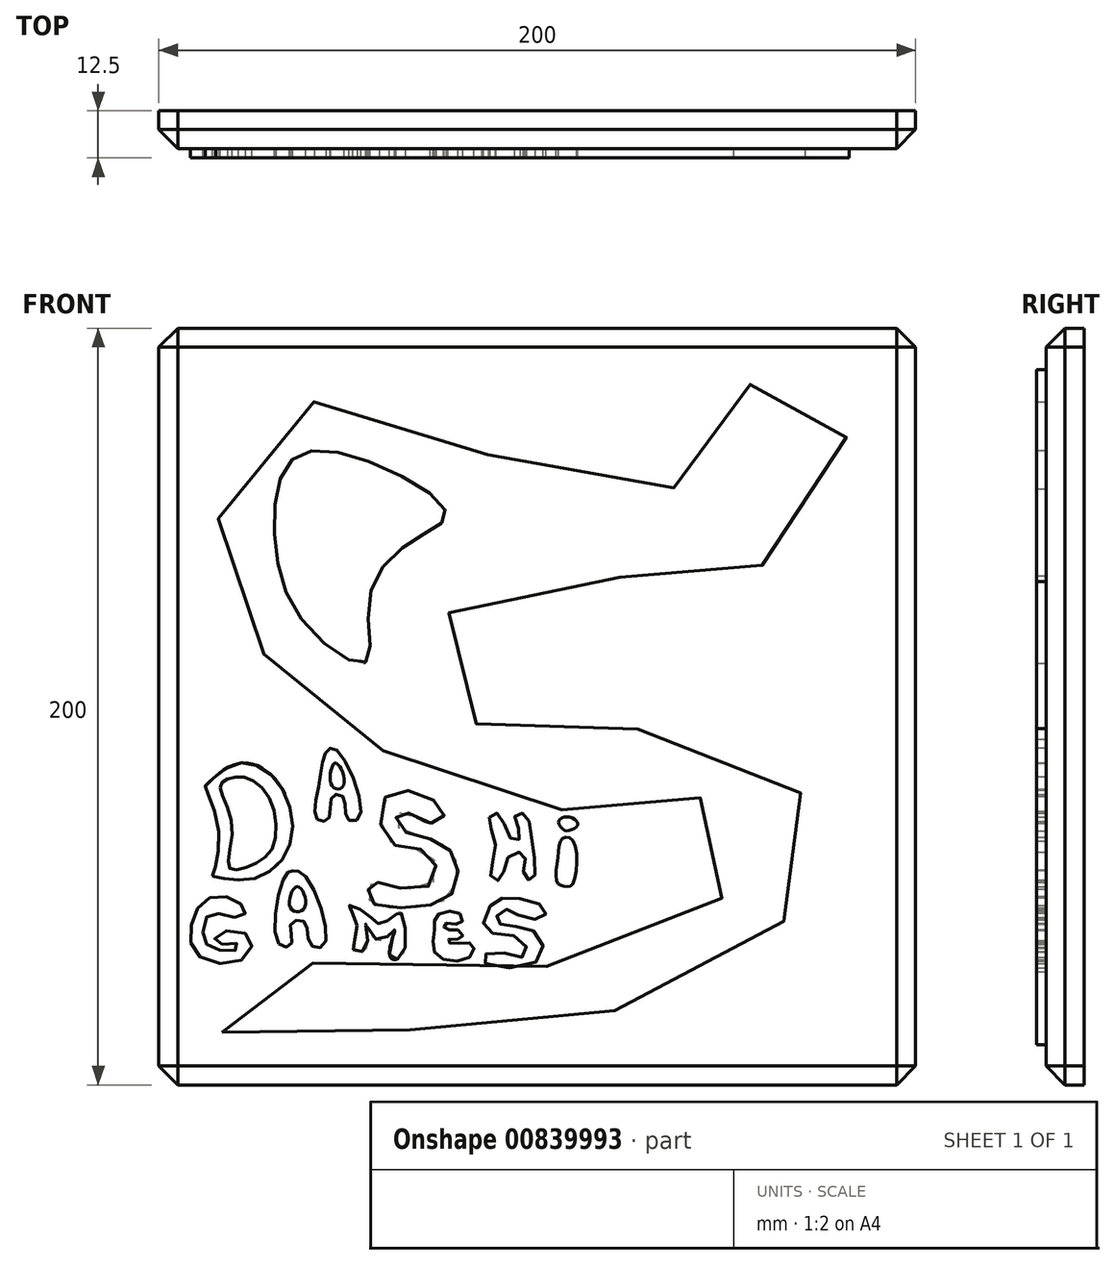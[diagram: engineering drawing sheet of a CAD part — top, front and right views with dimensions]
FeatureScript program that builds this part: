
annotation { "Feature Type Name" : "Feature", "Feature Type Description" : "" }
export const myFeature = defineFeature(function(context is Context, id is Id, definition is map)
    precondition{}
    {
        {
            var Q0;
            Q0=qCreatedBy(makeId("Front.planeOp"),FACE);
            var sketch = newSketch(context, id + "F0", { "sketchPlane" : qUnion([Q0])});
            skLineSegment(sketch, "E0.bottom", {"start": v(100, -100) * mm, "end": v(-100, -100) * mm});
            skLineSegment(sketch, "E0.top", {"start": v(100, 100) * mm, "end": v(-100, 100) * mm});
            skLineSegment(sketch, "E0.left", {"start": v(100, -100) * mm, "end": v(100, 100) * mm});
            skLineSegment(sketch, "E0.right", {"start": v(-100, -100) * mm, "end": v(-100, 100) * mm});
            skPoint(sketch, "E0.middle", {"position": v(0, 0) * mm});
            skLineSegment(sketch, "E1.bottom", {"start": v(95, -95) * mm, "end": v(-95, -95) * mm});
            skLineSegment(sketch, "E1.top", {"start": v(95, 95) * mm, "end": v(-95, 95) * mm});
            skLineSegment(sketch, "E1.left", {"start": v(95, -95) * mm, "end": v(95, 95) * mm});
            skLineSegment(sketch, "E1.right", {"start": v(-95, -95) * mm, "end": v(-95, 95) * mm});
            skSolve(sketch);
        }
        {
            var Q0;
            Q0=makeQuery(id+"F0.imprint","IMPRINT",FACE,{"disambiguationData":[TD([[makeQuery(id+"F0.imprint","IMPRINT",EDGE,{"derivedFrom":sQuery(id+"F0.wireOp",EDGE,"E0.bottom")}),-1.0]])]});
            var Q1;
            Q1=makeQuery(id+"F0.imprint","IMPRINT",FACE,{"disambiguationData":[TD([[makeQuery(id+"F0.imprint","IMPRINT",EDGE,{"derivedFrom":sQuery(id+"F0.wireOp",EDGE,"E1.bottom")}),-1.0]])]});
            extrude(context, id + "F1", {"entities" : qUnion([Q0, Q1]), "depth" : 10 * mm, "offsetDistance" : 25 * mm});
        }
        {
            var Q0;
            Q0=makeQuery(id+"F1.opExtrude","CAP_EDGE",EDGE,{"disambiguationData":[OSD([sQuery(id+"F0.wireOp",EDGE,"E0.right")])],"isStart":false});
            var Q1;
            Q1=makeQuery(id+"F1.opExtrude","CAP_EDGE",EDGE,{"disambiguationData":[OSD([sQuery(id+"F0.wireOp",EDGE,"E0.top")])],"isStart":false});
            var Q2;
            Q2=makeQuery(id+"F1.opExtrude","CAP_EDGE",EDGE,{"disambiguationData":[OSD([sQuery(id+"F0.wireOp",EDGE,"E0.left")])],"isStart":false});
            var Q3;
            Q3=makeQuery(id+"F1.opExtrude","CAP_EDGE",EDGE,{"disambiguationData":[OSD([sQuery(id+"F0.wireOp",EDGE,"E0.bottom")])],"isStart":false});
            var Q4;
            Q4=makeQuery(id+"F1.opExtrude","SWEPT_EDGE",EDGE,{"disambiguationData":[OSD([sQuery(id+"F0.wireOp",EDGE,"E0.bottom"),sQuery(id+"F0.wireOp",EDGE,"E0.right")])]});
            var Q5;
            Q5=makeQuery(id+"F1.opExtrude","SWEPT_EDGE",EDGE,{"disambiguationData":[OSD([sQuery(id+"F0.wireOp",EDGE,"E0.bottom"),sQuery(id+"F0.wireOp",EDGE,"E0.left")])]});
            var Q6;
            Q6=makeQuery(id+"F1.opExtrude","SWEPT_EDGE",EDGE,{"disambiguationData":[OSD([sQuery(id+"F0.wireOp",EDGE,"E0.top"),sQuery(id+"F0.wireOp",EDGE,"E0.left")])]});
            var Q7;
            Q7=makeQuery(id+"F1.opExtrude","SWEPT_EDGE",EDGE,{"disambiguationData":[OSD([sQuery(id+"F0.wireOp",EDGE,"E0.top"),sQuery(id+"F0.wireOp",EDGE,"E0.right")])]});
            chamfer(context, id + "F2", {"entities" : qUnion([Q0, Q1, Q2, Q3, Q4, Q5, Q6, Q7]), "width" : 5 * mm, "tangentPropagation" : true});
        }
        {
            var Q0;
            Q0=makeQuery(id+"F1.opExtrude","CAP_FACE",FACE,{"disambiguationData":[OSD([sQuery(id+"F0.wireOp",EDGE,"E0.bottom"),sQuery(id+"F0.wireOp",EDGE,"E0.top"),sQuery(id+"F0.wireOp",EDGE,"E0.left"),sQuery(id+"F0.wireOp",EDGE,"E0.right")])],"isStart":false});
            var sketch = newSketch(context, id + "F3", { "sketchPlane" : qUnion([Q0])});
            skFitSpline(sketch, "E2", {"points": [v(-83.32, -86.12) * mm, v(-48.42, -86.95) * mm, v(-5.86, -83.59) * mm, v(41.8, -74.11) * mm, v(67.33, -53.5) * mm, v(70.78, -37.14) * mm, v(66.85, -17.91) * mm, v(31.27, -5.86) * mm, v(0, -8.55) * mm, v(-22.54, 0) * mm, v(-28.05, 16.04) * mm, v(-14.35, 30.84) * mm, v(22.77, 34.18) * mm, v(46.79, 33.3) * mm, v(64.36, 40.75) * mm, v(78.67, 62.28) * mm, v(79.86, 84.4) * mm, v(57.44, 86.25) * mm, v(49.53, 65.7) * mm, v(33.87, 57.63) * mm, v(-6.5, 64.2) * mm, v(-31.83, 74.37) * mm, v(-70.9, 78.72) * mm, v(-83.6, 54.3) * mm, v(-82.52, 25.13) * mm, v(-68.7, 11.08) * mm, v(-49.09, -5.84) * mm, v(-25.34, -19.22) * mm, v(15.67, -27.72) * mm, v(35.5, -24.12) * mm, v(47.04, -26) * mm, v(51.9, -38.49) * mm, v(46.2, -53.9) * mm, v(9.44, -67.82) * mm, v(-51.38, -68.69) * mm, v(-79.23, -70.4) * mm, v(-83.32, -86.12) * mm]});
            skFitSpline(sketch, "E3", {"points": [v(-45.32, 11.8) * mm, v(-44.43, 28.48) * mm, v(-32.34, 44.24) * mm, v(-24.04, 51) * mm, v(-44.27, 64.7) * mm, v(-64.44, 65.6) * mm, v(-69.49, 47.62) * mm, v(-61.7, 22.33) * mm, v(-45.32, 11.8) * mm]});
            skFitSpline(sketch, "E4", {"points": [v(-87.76, -21.05) * mm, v(-84.2, -32.58) * mm, v(-85.74, -44.45) * mm, v(-85.82, -44.85) * mm, v(-85.1, -45.01) * mm, v(-76.16, -45.7) * mm, v(-65.81, -37.77) * mm, v(-67.57, -21.4) * mm, v(-78.95, -15) * mm, v(-87.22, -20.43) * mm, v(-87.67, -20.9) * mm, v(-87.7, -20.97) * mm, v(-87.76, -21.05) * mm]});
            skFitSpline(sketch, "E5", {"points": [v(-83.8, -21.43) * mm, v(-80.64, -31.67) * mm, v(-81.41, -42.59) * mm, v(-76.25, -42.24) * mm, v(-69.8, -36.97) * mm, v(-70.93, -24.01) * mm, v(-77.58, -18.62) * mm, v(-82.58, -19.54) * mm, v(-83.8, -21.43) * mm]});
            skFitSpline(sketch, "E6", {"points": [v(-58.2, -29.85) * mm, v(-57.67, -20.7) * mm, v(-55.7, -11.82) * mm, v(-53.04, -11.43) * mm, v(-46.97, -29.24) * mm, v(-50.2, -29.63) * mm, v(-51.18, -24) * mm, v(-54.23, -23.73) * mm, v(-55.06, -29.55) * mm, v(-58.2, -29.85) * mm]});
            skFitSpline(sketch, "E7", {"points": [v(-54.24, -20.97) * mm, v(-51.2, -20.77) * mm, v(-53.31, -14.96) * mm, v(-54.24, -20.97) * mm]});
            skFitSpline(sketch, "E8", {"points": [v(-28.02, -30.79) * mm, v(-24.6, -28.77) * mm, v(-29.67, -23.45) * mm, v(-40.24, -24.06) * mm, v(-38.95, -35.88) * mm, v(-28.75, -38.6) * mm, v(-27.95, -46.9) * mm, v(-40.42, -47.04) * mm, v(-43.75, -46.76) * mm, v(-44.5, -51.05) * mm, v(-34.5, -53.11) * mm, v(-22.7, -49.64) * mm, v(-21.5, -40.48) * mm, v(-27.72, -35.17) * mm, v(-36.87, -31.58) * mm, v(-36.23, -27.72) * mm, v(-28.02, -30.79) * mm]});
            skFitSpline(sketch, "E9", {"points": [v(-12.7, -29.26) * mm, v(-11.02, -36.44) * mm, v(-12.24, -45) * mm, v(-9.87, -45.7) * mm, v(-7.33, -39.45) * mm, v(-3.32, -39.17) * mm, v(-3.56, -44.57) * mm, v(-1.25, -45.7) * mm, v(-1.3, -35.94) * mm, v(-3.43, -28.44) * mm, v(-5.86, -28.84) * mm, v(-4.46, -34.43) * mm, v(-6.69, -35.17) * mm, v(-10.14, -28.4) * mm, v(-12.7, -29.26) * mm]});
            skFitSpline(sketch, "E10", {"points": [v(5.43, -39.9) * mm, v(5.27, -46.5) * mm, v(7.3, -47.45) * mm, v(9.36, -46.9) * mm, v(9.46, -35.49) * mm, v(6.7, -34.82) * mm, v(5.43, -39.9) * mm]});
            skFitSpline(sketch, "E11", {"points": [v(6.31, -31.89) * mm, v(7.62, -32.8) * mm, v(10.64, -31.39) * mm, v(8.52, -29.18) * mm, v(5.68, -30.25) * mm, v(6.31, -31.89) * mm]});
            skFitSpline(sketch, "E12", {"points": [v(-80.02, -55.73) * mm, v(-77.12, -54.4) * mm, v(-79.98, -51.05) * mm, v(-87.55, -51.02) * mm, v(-91.44, -58.18) * mm, v(-89.58, -65.83) * mm, v(-77.7, -66.73) * mm, v(-76.16, -60.65) * mm, v(-84.48, -60.18) * mm, v(-84.66, -62.64) * mm, v(-79.3, -62.69) * mm, v(-79.54, -64.27) * mm, v(-85.98, -63.66) * mm, v(-88.33, -60.63) * mm, v(-86.53, -54.8) * mm, v(-80.02, -55.73) * mm]});
            skFitSpline(sketch, "E13", {"points": [v(-68.33, -62.77) * mm, v(-65, -62.69) * mm, v(-65.09, -57.38) * mm, v(-61.39, -57) * mm, v(-59.98, -62.74) * mm, v(-56.21, -62.87) * mm, v(-61.3, -44.8) * mm, v(-64.64, -43.36) * mm, v(-66.8, -44.96) * mm, v(-68.33, -62.77) * mm]});
            skFitSpline(sketch, "E14", {"points": [v(-65.25, -53.1) * mm, v(-61.55, -53.3) * mm, v(-63.31, -47.57) * mm, v(-65.25, -53.1) * mm]});
            skFitSpline(sketch, "E15", {"points": [v(-48.55, -64.2) * mm, v(-47.53, -58.04) * mm, v(-49.74, -52.6) * mm, v(-44.47, -55.22) * mm, v(-41.65, -57.38) * mm, v(-37.18, -54.84) * mm, v(-36.04, -54.4) * mm, v(-35.64, -65.65) * mm, v(-38.95, -66.01) * mm, v(-37.7, -58.97) * mm, v(-41.9, -61.8) * mm, v(-45.32, -57.38) * mm, v(-45.32, -64.01) * mm, v(-48.55, -64.2) * mm]});
            skFitSpline(sketch, "E16", {"points": [v(-20.42, -54.7) * mm, v(-26.47, -55.15) * mm, v(-27.16, -59.2) * mm, v(-26.69, -65.62) * mm, v(-17.82, -66.2) * mm, v(-17.4, -62.6) * mm, v(-22.84, -62.61) * mm, v(-23.55, -61.65) * mm, v(-19.86, -61.1) * mm, v(-20.84, -59.09) * mm, v(-24.26, -58.84) * mm, v(-24.44, -57.38) * mm, v(-20.32, -57.38) * mm, v(-20.42, -54.7) * mm]});
            skFitSpline(sketch, "E17", {"points": [v(-5.05, -55.12) * mm, v(1.52, -55.76) * mm, v(1.87, -53.11) * mm, v(-6.76, -50.54) * mm, v(-12.12, -52.3) * mm, v(-13.66, -59.02) * mm, v(-4.36, -61.28) * mm, v(-3.32, -65.98) * mm, v(-11.47, -64.75) * mm, v(-14.47, -67.3) * mm, v(0, -67.3) * mm, v(0, -60.12) * mm, v(-7.63, -57.9) * mm, v(-10.96, -56.41) * mm, v(-8.74, -53.68) * mm, v(-5.05, -55.12) * mm]});
            skSolve(sketch);
        }
        {
            var Q0;
            Q0=makeQuery(id+"F3.imprint","IMPRINT",FACE,{"disambiguationData":[TD([[makeQuery(id+"F3.imprint","IMPRINT",EDGE,{"derivedFrom":sQuery(id+"F3.wireOp",EDGE,"E4")}),1.0]])]});
            var Q1;
            Q1=makeQuery(id+"F3.imprint","IMPRINT",FACE,{"disambiguationData":[TD([[makeQuery(id+"F3.imprint","IMPRINT",EDGE,{"derivedFrom":sQuery(id+"F3.wireOp",EDGE,"E6")}),-1.0]])]});
            var Q2;
            Q2=makeQuery(id+"F3.imprint","IMPRINT",FACE,{"disambiguationData":[TD([[makeQuery(id+"F3.imprint","IMPRINT",EDGE,{"derivedFrom":sQuery(id+"F3.wireOp",EDGE,"E8")}),1.0]])]});
            var Q3;
            Q3=makeQuery(id+"F3.imprint","IMPRINT",FACE,{"disambiguationData":[TD([[makeQuery(id+"F3.imprint","IMPRINT",EDGE,{"derivedFrom":sQuery(id+"F3.wireOp",EDGE,"E9")}),1.0]])]});
            var Q4;
            Q4=makeQuery(id+"F3.imprint","IMPRINT",FACE,{"disambiguationData":[TD([[makeQuery(id+"F3.imprint","IMPRINT",EDGE,{"derivedFrom":sQuery(id+"F3.wireOp",EDGE,"E10")}),1.0]])]});
            var Q5;
            Q5=makeQuery(id+"F3.imprint","IMPRINT",FACE,{"disambiguationData":[TD([[makeQuery(id+"F3.imprint","IMPRINT",EDGE,{"derivedFrom":sQuery(id+"F3.wireOp",EDGE,"E11")}),1.0]])]});
            var Q6;
            Q6=makeQuery(id+"F3.imprint","IMPRINT",FACE,{"disambiguationData":[TD([[makeQuery(id+"F3.imprint","IMPRINT",EDGE,{"derivedFrom":sQuery(id+"F3.wireOp",EDGE,"E16")}),1.0]])]});
            var Q7;
            Q7=makeQuery(id+"F3.imprint","IMPRINT",FACE,{"disambiguationData":[TD([[makeQuery(id+"F3.imprint","IMPRINT",EDGE,{"derivedFrom":sQuery(id+"F3.wireOp",EDGE,"E17")}),1.0]])]});
            var Q8;
            Q8=makeQuery(id+"F3.imprint","IMPRINT",FACE,{"disambiguationData":[TD([[makeQuery(id+"F3.imprint","IMPRINT",EDGE,{"derivedFrom":sQuery(id+"F3.wireOp",EDGE,"E15")}),-1.0]])]});
            var Q9;
            Q9=makeQuery(id+"F3.imprint","IMPRINT",FACE,{"disambiguationData":[TD([[makeQuery(id+"F3.imprint","IMPRINT",EDGE,{"derivedFrom":sQuery(id+"F3.wireOp",EDGE,"E13")}),1.0]])]});
            var Q10;
            Q10=makeQuery(id+"F3.imprint","IMPRINT",FACE,{"disambiguationData":[TD([[makeQuery(id+"F3.imprint","IMPRINT",EDGE,{"derivedFrom":sQuery(id+"F3.wireOp",EDGE,"E12")}),1.0]])]});
            var Q11;
            Q11=makeQuery(id+"F3.imprint","IMPRINT",FACE,{"disambiguationData":[TD([[makeQuery(id+"F3.imprint","IMPRINT",EDGE,{"derivedFrom":sQuery(id+"F3.wireOp",EDGE,"E2")}),1.0]])]});
            extrude(context, id + "F4", {"entities" : qUnion([Q0, Q1, Q2, Q3, Q4, Q5, Q6, Q7, Q8, Q9, Q10, Q11]), "operationType" : NewBodyOperationType.ADD, "depth" : 2.5 * mm, "offsetDistance" : 25 * mm});
        }
    });
